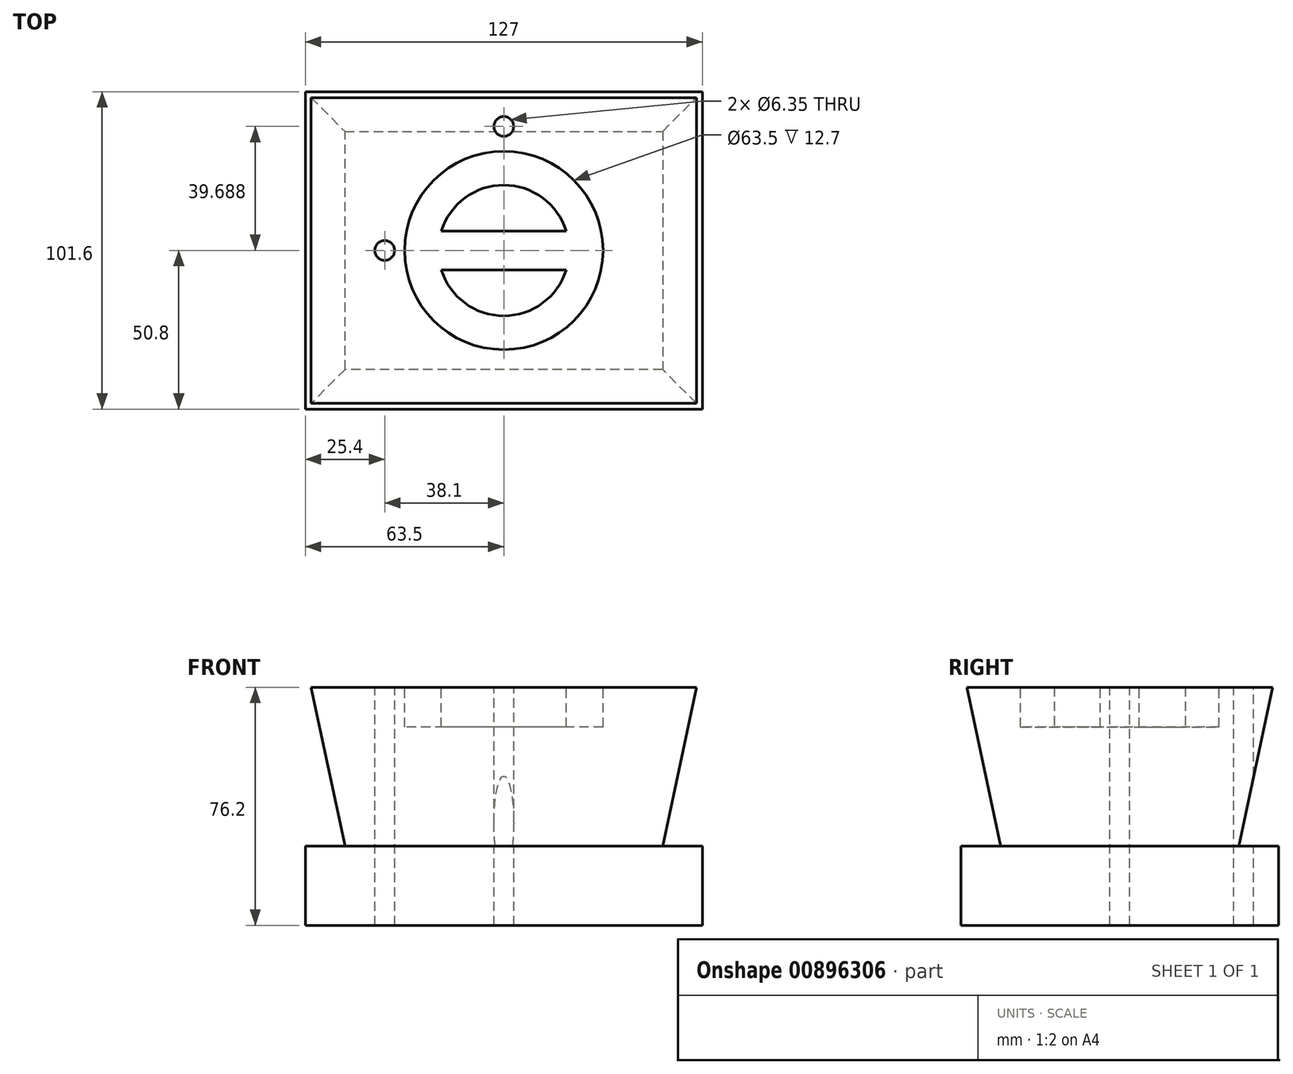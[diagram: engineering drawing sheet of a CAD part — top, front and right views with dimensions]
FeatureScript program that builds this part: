
annotation { "Feature Type Name" : "Feature", "Feature Type Description" : "" }
export const myFeature = defineFeature(function(context is Context, id is Id, definition is map)
    precondition{}
    {
        {
            var Q0;
            Q0=qCreatedBy(makeId("Top.planeOp"),FACE);
            var sketch = newSketch(context, id + "F0", { "sketchPlane" : qUnion([Q0])});
            skLineSegment(sketch, "E0.bottom", {"start": v(-63.5, -50.8) * mm, "end": v(63.5, -50.8) * mm});
            skLineSegment(sketch, "E0.top", {"start": v(-63.5, 50.8) * mm, "end": v(63.5, 50.8) * mm});
            skLineSegment(sketch, "E0.left", {"start": v(-63.5, -50.8) * mm, "end": v(-63.5, 50.8) * mm});
            skLineSegment(sketch, "E0.right", {"start": v(63.5, -50.8) * mm, "end": v(63.5, 50.8) * mm});
            skSolve(sketch);
        }
        {
            var Q0;
            Q0 = qSketchRegion(id + "F0", true);
            extrude(context, id + "F1", {"entities" : qUnion([Q0]), "depth" : 25.4 * mm, "offsetDistance" : 25.4 * mm});
        }
        {
            var Q0;
            Q0=makeQuery(id+"F1.opExtrude","CAP_FACE",FACE,{"disambiguationData":[OSD([sQuery(id+"F0.wireOp",EDGE,"E0.bottom"),sQuery(id+"F0.wireOp",EDGE,"E0.top"),sQuery(id+"F0.wireOp",EDGE,"E0.left"),sQuery(id+"F0.wireOp",EDGE,"E0.right")])],"isStart":false});
            var sketch = newSketch(context, id + "F2", { "sketchPlane" : qUnion([Q0])});
            skLineSegment(sketch, "E1.bottom", {"start": v(50.8, 38.1) * mm, "end": v(-50.8, 38.1) * mm});
            skLineSegment(sketch, "E1.top", {"start": v(50.8, -38.1) * mm, "end": v(-50.8, -38.1) * mm});
            skLineSegment(sketch, "E1.left", {"start": v(50.8, 38.1) * mm, "end": v(50.8, -38.1) * mm});
            skLineSegment(sketch, "E1.right", {"start": v(-50.8, 38.1) * mm, "end": v(-50.8, -38.1) * mm});
            skPoint(sketch, "E1.middle", {"position": v(0, 0) * mm});
            skSolve(sketch);
        }
        {
            var Q0;
            Q0 = qSketchRegion(id + "F2", true);
            extrude(context, id + "F3", {"entities" : qUnion([Q0]), "operationType" : NewBodyOperationType.ADD, "depth" : 50.8 * mm, "offsetDistance" : 25.4 * mm, "hasDraft" : true, "draftAngle" : 12 * degree});
        }
        {
            var Q0;
            Q0=makeQuery(id+"F3.opExtrude","CAP_FACE",FACE,{"disambiguationData":[OSD([sQuery(id+"F2.wireOp",EDGE,"E1.bottom"),sQuery(id+"F2.wireOp",EDGE,"E1.top"),sQuery(id+"F2.wireOp",EDGE,"E1.left"),sQuery(id+"F2.wireOp",EDGE,"E1.right")])],"isStart":false});
            var sketch = newSketch(context, id + "F4", { "sketchPlane" : qUnion([Q0])});
            skCircle(sketch, "E2", {"center": v(0, 0) * mm, "radius": 31.75 * mm});
            skSolve(sketch);
        }
        {
            var Q0;
            Q0 = qSketchRegion(id + "F4", true);
            extrude(context, id + "F5", {"entities" : qUnion([Q0]), "operationType" : NewBodyOperationType.REMOVE, "oppositeDirection" : true, "depth" : 12.7 * mm, "offsetDistance" : 25.4 * mm});
        }
        {
            var Q0;
            Q0=makeQuery(id+"F5.boolean.opBoolean","COPY",FACE,{"derivedFrom":makeQuery(id+"F5.opExtrude","CAP_FACE",FACE,{"disambiguationData":[OSD([sQuery(id+"F4.wireOp",EDGE,"E2")])],"isStart":false})});
            var sketch = newSketch(context, id + "F6", { "sketchPlane" : qUnion([Q0])});
            skCircle(sketch, "E3", {"center": v(0, 0) * mm, "radius": 20.93 * mm});
            skLineSegment(sketch, "E4.bottom", {"start": v(-66.67, 53.98) * mm, "end": v(66.68, 53.98) * mm, "construction": true});
            skLineSegment(sketch, "E4.top", {"start": v(-66.67, -53.98) * mm, "end": v(66.68, -53.98) * mm, "construction": true});
            skLineSegment(sketch, "E4.left", {"start": v(-66.67, 53.98) * mm, "end": v(-66.67, -53.98) * mm, "construction": true});
            skLineSegment(sketch, "E4.right", {"start": v(66.68, 53.98) * mm, "end": v(66.68, -53.98) * mm, "construction": true});
            skSolve(sketch);
        }
        {
            var Q0;
            Q0 = qSketchRegion(id + "F6", true);
            extrude(context, id + "F7", {"entities" : qUnion([Q0]), "operationType" : NewBodyOperationType.ADD, "depth" : 12.7 * mm, "offsetDistance" : 25.4 * mm});
        }
        {
            var Q0;
            Q0=makeQuery(id+"F3.opExtrude","CAP_FACE",FACE,{"disambiguationData":[OSD([sQuery(id+"F2.wireOp",EDGE,"E1.bottom"),sQuery(id+"F2.wireOp",EDGE,"E1.top"),sQuery(id+"F2.wireOp",EDGE,"E1.left"),sQuery(id+"F2.wireOp",EDGE,"E1.right")])],"isStart":false});
            var sketch = newSketch(context, id + "F8", { "sketchPlane" : qUnion([Q0])});
            skCircle(sketch, "E5", {"center": v(-38.1, 0) * mm, "radius": 3.18 * mm});
            skCircle(sketch, "E6", {"center": v(0, 39.69) * mm, "radius": 3.18 * mm});
            skLineSegment(sketch, "E7.bottom", {"start": v(66.68, 53.97) * mm, "end": v(-66.68, 53.98) * mm, "construction": true});
            skLineSegment(sketch, "E7.top", {"start": v(66.68, -53.98) * mm, "end": v(-66.68, -53.97) * mm, "construction": true});
            skLineSegment(sketch, "E7.left", {"start": v(66.68, 53.97) * mm, "end": v(66.67, -53.98) * mm, "construction": true});
            skLineSegment(sketch, "E7.right", {"start": v(-66.68, 53.98) * mm, "end": v(-66.68, -53.97) * mm, "construction": true});
            skPoint(sketch, "E7.middle", {"position": v(0, 0) * mm});
            skLineSegment(sketch, "E8", {"start": v(-38.1, 0) * mm, "end": v(0, 0) * mm, "construction": true});
            skLineSegment(sketch, "E9", {"start": v(0, 39.69) * mm, "end": v(0, 0) * mm, "construction": true});
            skSolve(sketch);
        }
        {
            var Q0;
            Q0 = qSketchRegion(id + "F8", true);
            extrude(context, id + "F9", {"entities" : qUnion([Q0]), "operationType" : NewBodyOperationType.REMOVE, "endBound" : BoundingType.THROUGH_ALL, "oppositeDirection" : true, "depth" : 25.4 * mm, "offsetDistance" : 25.4 * mm});
        }
        {
            var Q0;
            Q0=makeQuery(id+"F3.opExtrude","CAP_FACE",FACE,{"disambiguationData":[OSD([sQuery(id+"F2.wireOp",EDGE,"E1.bottom"),sQuery(id+"F2.wireOp",EDGE,"E1.top"),sQuery(id+"F2.wireOp",EDGE,"E1.left"),sQuery(id+"F2.wireOp",EDGE,"E1.right")])],"isStart":false});
            var sketch = newSketch(context, id + "F10", { "sketchPlane" : qUnion([Q0])});
            skLineSegment(sketch, "E10.bottom", {"start": v(20, 6.2) * mm, "end": v(-20, 6.2) * mm});
            skLineSegment(sketch, "E10.top", {"start": v(20, -6.2) * mm, "end": v(-20, -6.2) * mm});
            skPoint(sketch, "E10.middle", {"position": v(0, 0) * mm});
            skLineSegment(sketch, "E11", {"start": v(-20, 6.2) * mm, "end": v(-20, 6.2) * mm});
            skArc(sketch, "E12", {"start": v(20, 6.2) * mm, "mid": v(20.93, 0) * mm, "end": v(20, -6.2) * mm});
            skArc(sketch, "E13", {"start": v(-20, 6.2) * mm, "mid": v(-20.93, 0) * mm, "end": v(-20, -6.2) * mm});
            skSolve(sketch);
        }
        {
            var Q0;
            Q0 = qSketchRegion(id + "F10", true);
            extrude(context, id + "F11", {"entities" : qUnion([Q0]), "operationType" : NewBodyOperationType.REMOVE, "oppositeDirection" : true, "depth" : 12.7 * mm, "offsetDistance" : 25.4 * mm});
        }
    });
